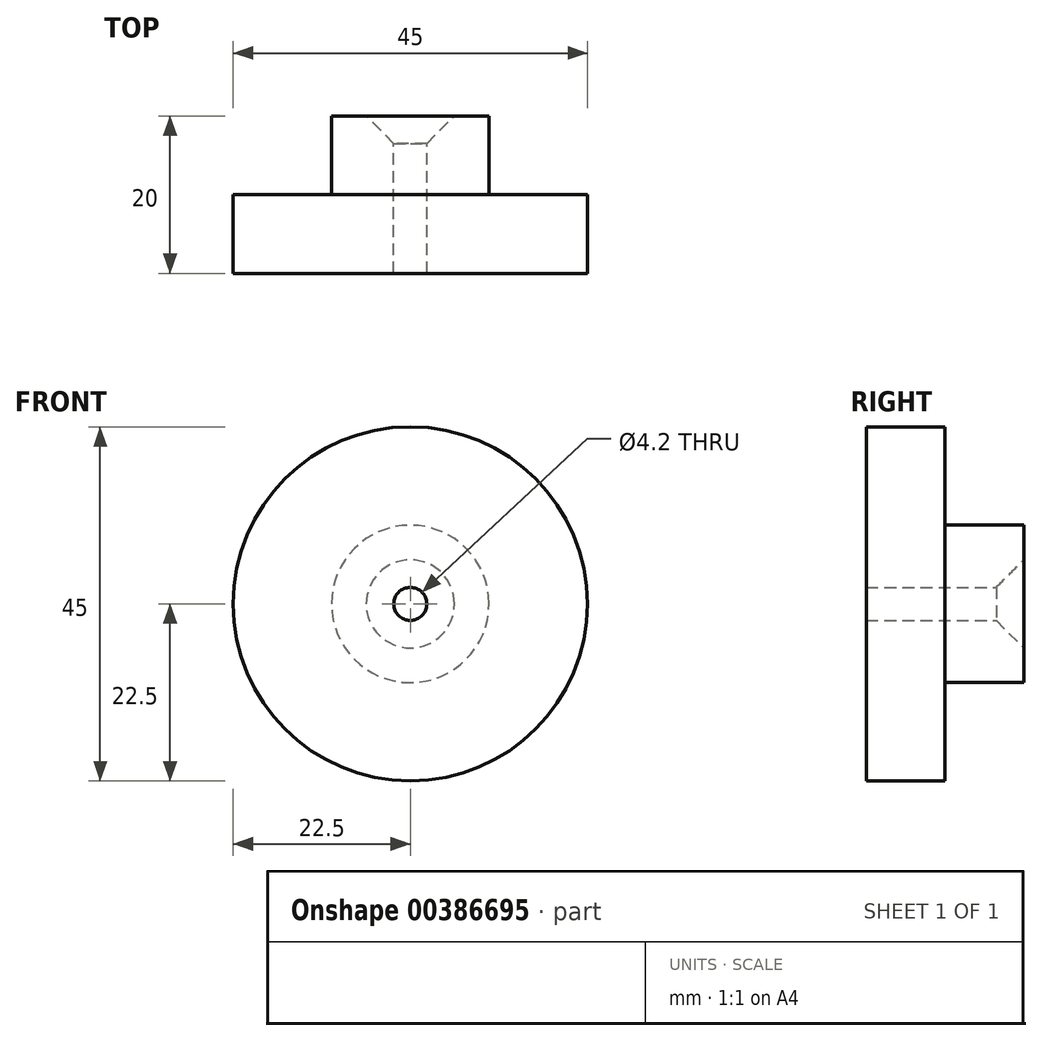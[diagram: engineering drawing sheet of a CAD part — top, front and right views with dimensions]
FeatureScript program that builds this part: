
annotation { "Feature Type Name" : "Feature", "Feature Type Description" : "" }
export const myFeature = defineFeature(function(context is Context, id is Id, definition is map)
    precondition{}
    {
        {
            var Q0;
            Q0=qCreatedBy(makeId("Front.planeOp"),FACE);
            var sketch = newSketch(context, id + "F0", { "sketchPlane" : qUnion([Q0])});
            skCircle(sketch, "E0", {"center": v(0, 0) * mm, "radius": 22.5 * mm});
            skSolve(sketch);
        }
        {
            var Q0;
            Q0 = qSketchRegion(id + "F0", true);
            extrude(context, id + "F1", {"entities" : qUnion([Q0]), "depth" : 10 * mm});
        }
        {
            var Q0;
            Q0=makeQuery(id+"F1.opExtrude","CAP_FACE",FACE,{"disambiguationData":[OSD([sQuery(id+"F0.wireOp",EDGE,"E0")])],"isStart":true});
            var sketch = newSketch(context, id + "F2", { "sketchPlane" : qUnion([Q0])});
            skCircle(sketch, "E1", {"center": v(0, 0) * mm, "radius": 10 * mm});
            skSolve(sketch);
        }
        {
            var Q0;
            Q0 = qSketchRegion(id + "F2", true);
            extrude(context, id + "F3", {"entities" : qUnion([Q0]), "operationType" : NewBodyOperationType.ADD, "depth" : 10 * mm});
        }
        {
            var Q0;
            Q0=makeQuery(id+"F3.opExtrude","CAP_FACE",FACE,{"disambiguationData":[OSD([sQuery(id+"F2.wireOp",EDGE,"E1")])],"isStart":false});
            var sketch = newSketch(context, id + "F4", { "sketchPlane" : qUnion([Q0])});
            skPoint(sketch, "E2", {"position": v(0, 0) * mm});
            skSolve(sketch);
        }
        {
            var Q0;
            Q0=sQuery(id+"F4.wireOp",VERTEX,"E2");
            var Q1;
            Q1=makeQuery(id+"F1.opExtrude","SWEPT_BODY",BODY,{"disambiguationData":[OSD([sQuery(id+"F0.wireOp",EDGE,"E0")])]});
            hole(context, id + "F5", {"style" : HoleStyle.C_SINK, "endStyle" : HoleEndStyle.THROUGH, "standardTappedOrClearance" : lookupTablePath({ "standard" : "ISO", "engagement" : "75%", "pitch" : "0.8 mm", "size" : "M5", "type" : "Tapped" }), "standardBlindInLast" : lookupTablePath({ "standard" : "ISO", "engagement" : "75%", "pitch" : "0.8 mm", "size" : "M5", "type" : "Tapped" }), "holeDiameter" : 4.2 * mm, "cSinkDiameter" : 11.2 * mm, "cSinkAngle" : 90 * degree, "showTappedDepth" : true, "isTappedThrough" : true, "tappedDepth" : 12 * mm, "tapClearance" : 3, "locations" : qUnion([Q0]), "scope" : qUnion([Q1]), "majorDiameter" : 5 * mm});
        }
    });
